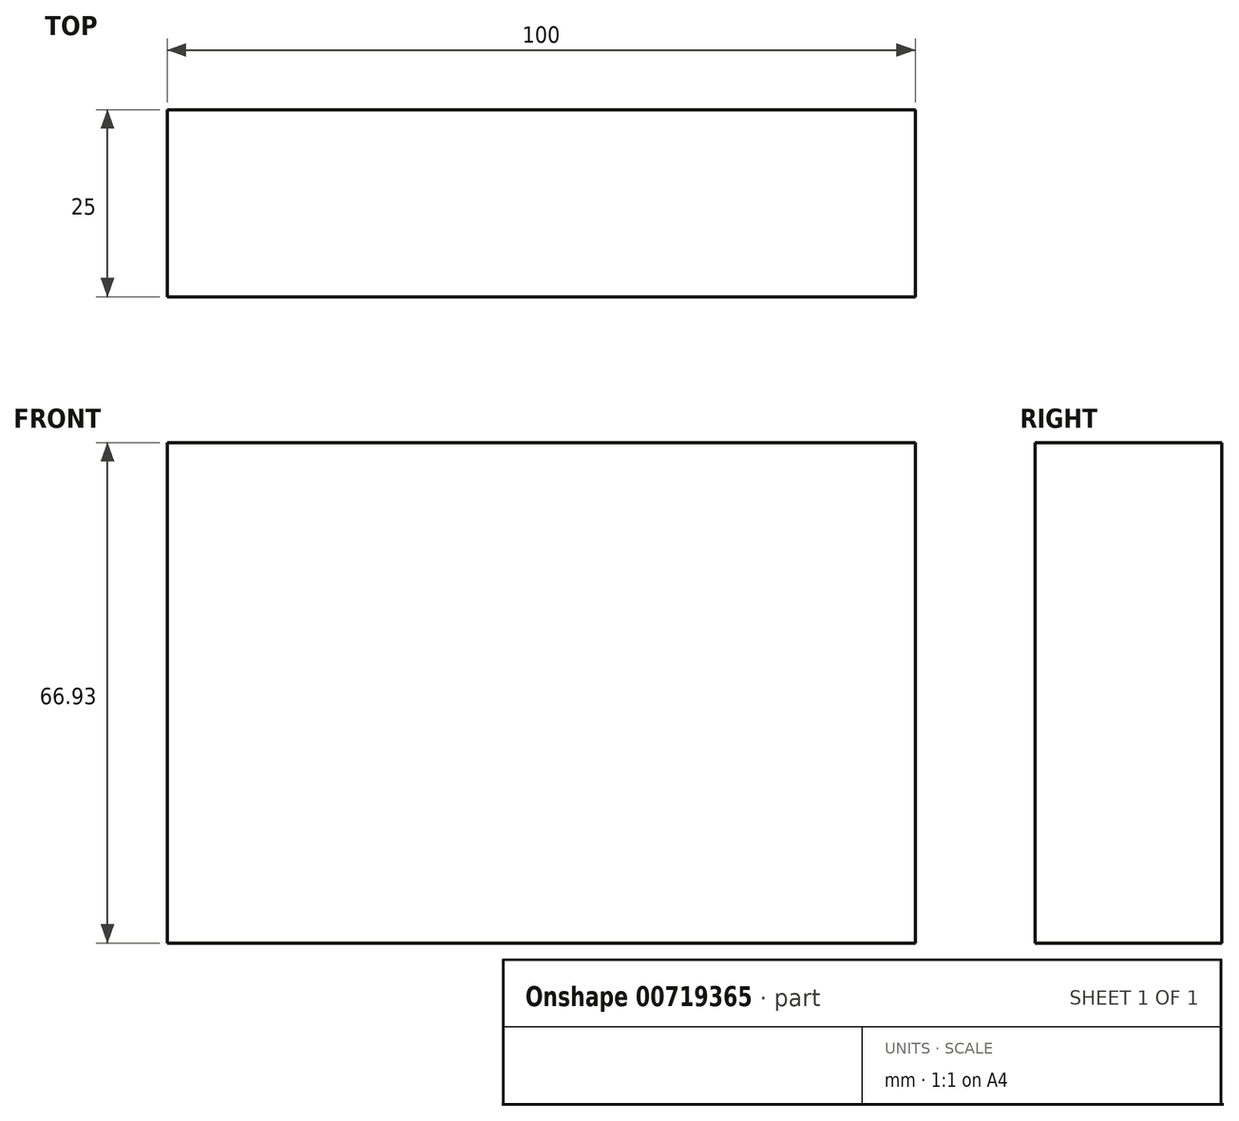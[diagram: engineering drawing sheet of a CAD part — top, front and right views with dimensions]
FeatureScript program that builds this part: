
annotation { "Feature Type Name" : "Feature", "Feature Type Description" : "" }
export const myFeature = defineFeature(function(context is Context, id is Id, definition is map)
    precondition{}
    {
        {
            var Q0;
            Q0=qCreatedBy(makeId("Front.planeOp"),FACE);
            var sketch = newSketch(context, id + "F0", { "sketchPlane" : qUnion([Q0])});
            skLineSegment(sketch, "E0", {"start": v(-45.2, 43.87) * mm, "end": v(36.93, 15.33) * mm});
            skLineSegment(sketch, "E1", {"start": v(36.93, 15.33) * mm, "end": v(26.56, 18.94) * mm});
            skLineSegment(sketch, "E2", {"start": v(26.56, 18.94) * mm, "end": v(16.67, -22.53) * mm});
            skLineSegment(sketch, "E3.bottom", {"start": v(-50.27, 22.8) * mm, "end": v(49.73, 22.8) * mm});
            skLineSegment(sketch, "E3.top", {"start": v(-50.27, -44.13) * mm, "end": v(49.73, -44.13) * mm});
            skLineSegment(sketch, "E3.left", {"start": v(-50.27, 22.8) * mm, "end": v(-50.27, -44.13) * mm});
            skLineSegment(sketch, "E3.right", {"start": v(49.73, 22.8) * mm, "end": v(49.73, -44.13) * mm});
            skSolve(sketch);
        }
        {
            var Q0;
            Q0=makeQuery(id+"F0.imprint","IMPRINT",FACE,{"disambiguationData":[TD([[makeQuery(id+"F0.imprint","IMPRINT",EDGE,{"derivedFrom":sQuery(id+"F0.wireOp",EDGE,"E3.top")}),1.0]])]});
            extrude(context, id + "F1", {"entities" : qUnion([Q0]), "depth" : 25 * mm, "offsetDistance" : 25 * mm});
        }
    });
